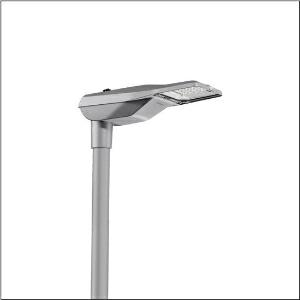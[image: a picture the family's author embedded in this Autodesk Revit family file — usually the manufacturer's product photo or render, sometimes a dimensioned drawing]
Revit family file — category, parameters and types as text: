
# Revit family: streetlight_sl_21_micro___pl52_5xe1h33s08db_2be5
name_source: partatom
category: Lighting Fixtures
units: mm (PartAtom-declared; Revit-internal decimal feet)

## family parameters
Cut with Voids When Loaded = No
Host = Face
Light Source = No
Part Type = Normal
Room Calculation Point = No
Round Connector Dimension = Use Diameter
Shared = No

## types (1)
- --- (1 x LED, 5020 lm, 39.1 W, 3000K)
    Apparent Load = 39 VA
    CIE Flux Codes = 27 59 98 100 100
    Color Rendering = 70
    Color Temperature = 3000K
    Default Elevation = 1800 mm
    Description = Streetlight SL 21 micro, mast luminaire, primary light control with lens, of PMMA, primary optical cover: cover, of toughened safety glass, transparent, light distribution: PL52, light emission: direct distribution, primary light characteristic: asymmetric, installation type: side-entry, post-top, LED, High Power LED, rated luminous flux: 5.020lm, luminous efficacy: 128lm/W, light colour: 730, colour temperature: 3000K, control: flexible luminous flux parameterisation, time-dependent luminous flux control, constant luminous flux control, overheat protection, presetting dimming logarithmic, mains connection: 220..240V, AC, 50/60Hz, start of lifetime: 39W, end of service life: 41W, reduction: 18W, luminaire housing, of diecast aluminium, powder-coated, Siteco® metallic grey (DB 702S), corrosivity category C5 mid according to DIN EN ISO 12944, please order mast flange separately, inclination adjustable: 0°, 5°, 10°, 15°, sealing non-destructively replaceable, multi-level sealing system, length: 528mm, width: 235mm, height: 110mm, mast flange for spigot size: 42mm (side-entry): 5XC10008XM4, 60/48mm (side-entry/post-top): 5XC10108XM2, 76/60mm (side-entry/post-top): 5XC10108XM1, Smart Interface above, protection rating (complete): IP66, insulation class (complete): insulation class II (safety insulation), certification: CE, ENEC, ENEC+, VDE, impact resistance: IK09, permissible operating ambient temperature for outdoor applications: -40..+50°C, standard-compliant lighting for roads and squares, packaging unit: 1 piece

Light Distribution: PL52
    Height = 110 mm
    Lamp = 1 x LED
    Lamp Light Flux = 5020 lm
    Lamp Power = 39.1 W
    Lamp count = 1
    Length = 528 mm
    Luminous efficacy = 128 lm/W
    Manufacturer = Siteco
    ModVariant = No
    Model = 5XE1H33S08DB
    Number of Poles = 1
    OnlyDefault = Yes
    Power Factor = 1
    Product Name = Streetlight SL 21 micro | PL52
    Product group = mast luminaire | pylon top
    ProductGroupID = 6100
    Protection Class = Protection class II
    Protection Degree = IP 66
    RLX_Detail_Level = 1
    RLX_Emergency_Light_Flux = 0 lm
    RLX_Emergency_Type = 0
    RLX_Emergency_Type_DB = No
    RlxData = <blob elided: 107753 chars, md5=56aef865>
    Socket = socket
    Standby Power = 0 W
    System Light Flux = 5020 lm
    System Power = 39 W
    Type Comments = factory setting: luminous flux: 100 % | dim-lin: 254 | 765 mA
    Type Image = l_1277292.jpg
    URL = http://relux.com
    VarID = @adj_106405
    Voltage = 0 V
    Weight = 0.00 kg
    Width = 235 mm

## geometry (parser evidence)
native form markers: Blend x4, Sweep x12
no freeform markers — native parametric forms only
